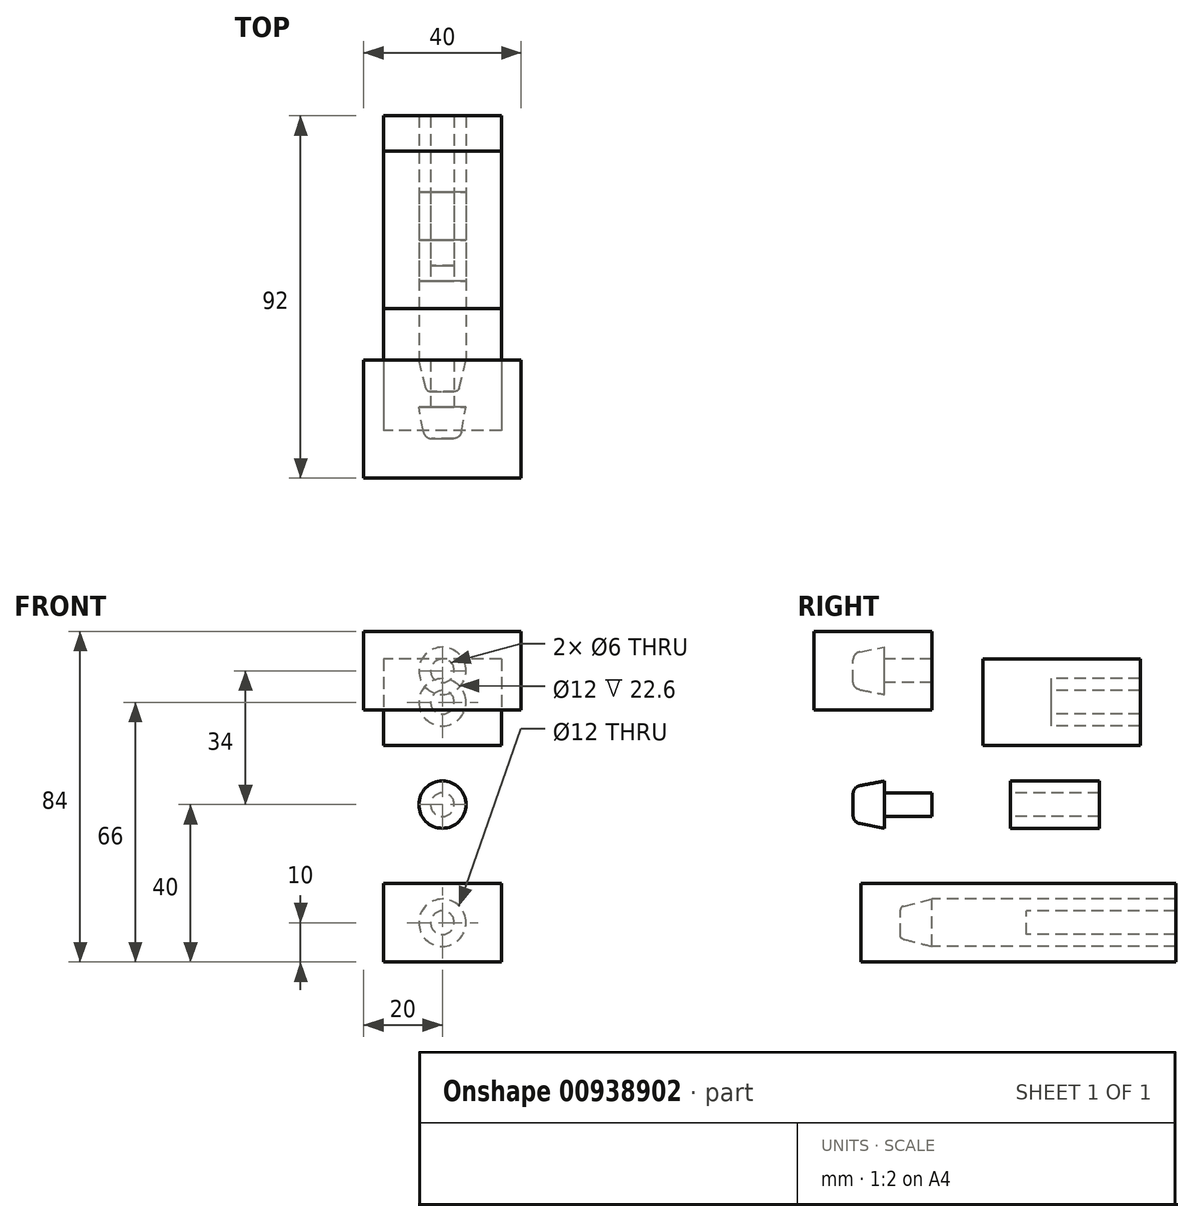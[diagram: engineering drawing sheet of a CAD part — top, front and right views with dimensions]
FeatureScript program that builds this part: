
annotation { "Feature Type Name" : "Feature", "Feature Type Description" : "" }
export const myFeature = defineFeature(function(context is Context, id is Id, definition is map)
    precondition{}
    {
        {
            var Q0;
            Q0=qCreatedBy(makeId("Right.planeOp"),FACE);
            var sketch = newSketch(context, id + "F0", { "sketchPlane" : qUnion([Q0])});
            skLineSegment(sketch, "E0.bottom", {"start": v(0, 0) * mm, "end": v(-12, 0) * mm});
            skLineSegment(sketch, "E0.top", {"start": v(0, 3) * mm, "end": v(-12, 3) * mm});
            skLineSegment(sketch, "E0.left", {"start": v(0, 0) * mm, "end": v(0, 3) * mm});
            skLineSegment(sketch, "E0.right", {"start": v(-12, 0) * mm, "end": v(-12, 3) * mm});
            skLineSegment(sketch, "E1.bottom", {"start": v(-12, 0) * mm, "end": v(-20, 0) * mm});
            skLineSegment(sketch, "E1.left", {"start": v(-12, 0) * mm, "end": v(-12, 6) * mm});
            skLineSegment(sketch, "E1.right", {"start": v(-20, 0) * mm, "end": v(-20, 4.5) * mm});
            skLineSegment(sketch, "E2", {"start": v(-12, 6) * mm, "end": v(-20, 4.5) * mm});
            skLineSegment(sketch, "E3", {"start": v(-20, 4.5) * mm, "end": v(-20, 6) * mm, "construction": true});
            skLineSegment(sketch, "E4", {"start": v(-20, 6) * mm, "end": v(-12, 6) * mm, "construction": true});
            skSolve(sketch);
        }
        {
            var Q0;
            Q0=makeQuery(id+"F0.imprint","IMPRINT",FACE,{"disambiguationData":[TD([[makeQuery(id+"F0.imprint","IMPRINT",EDGE,{"derivedFrom":sQuery(id+"F0.wireOp",EDGE,"E0.right")}),1.0]])]});
            var Q1;
            Q1=makeQuery(id+"F0.imprint","IMPRINT",FACE,{"disambiguationData":[TD([[makeQuery(id+"F0.imprint","IMPRINT",EDGE,{"derivedFrom":sQuery(id+"F0.wireOp",EDGE,"E0.bottom")}),-1.0]])]});
            var Q2;
            Q2=sQuery(id+"F0.wireOp",EDGE,"E0.bottom");
            revolve(context, id + "F1", {"surfaceOperationType" : NewSurfaceOperationType.NEW, "entities" : qUnion([Q0, Q1]), "axis" : qUnion([Q2]), "revolveType" : RevolveType.FULL});
        }
        {
            var Q0;
            Q0=qCreatedBy(makeId("Right.planeOp"),FACE);
            var sketch = newSketch(context, id + "F2", { "sketchPlane" : qUnion([Q0])});
            skLineSegment(sketch, "E5.bottom", {"start": v(20, 0) * mm, "end": v(42.6, 0) * mm});
            skLineSegment(sketch, "E5.top", {"start": v(20, 6) * mm, "end": v(42.6, 6) * mm});
            skLineSegment(sketch, "E5.left", {"start": v(20, 0) * mm, "end": v(20, 6) * mm});
            skLineSegment(sketch, "E5.right", {"start": v(42.6, 0) * mm, "end": v(42.6, 6) * mm});
            skLineSegment(sketch, "E6.top", {"start": v(20, 3) * mm, "end": v(42.6, 3) * mm});
            skLineSegment(sketch, "E6.left", {"start": v(20, 0) * mm, "end": v(20, 3) * mm});
            skLineSegment(sketch, "E6.right", {"start": v(42.6, 0) * mm, "end": v(42.6, 3) * mm});
            skSolve(sketch);
        }
        {
            var Q0;
            {var subQ0=sQuery(id+"F2.wireOp",EDGE,"E5.top");Q0=makeQuery(id+"F2.imprint","IMPRINT",FACE,{"disambiguationData":[TD([[makeQuery(id+"F2.imprint","IMPRINT",EDGE,{"derivedFrom":subQ0}),-1.0]])]});}
            var Q1;
            Q1=sQuery(id+"F2.wireOp",EDGE,"E5.bottom");
            revolve(context, id + "F3", {"surfaceOperationType" : NewSurfaceOperationType.NEW, "entities" : qUnion([Q0]), "axis" : qUnion([Q1]), "revolveType" : RevolveType.FULL});
        }
        {
            var Q0;
            Q0=qCreatedBy(makeId("Right.planeOp"),FACE);
            var sketch = newSketch(context, id + "F4", { "sketchPlane" : qUnion([Q0])});
            skLineSegment(sketch, "E7.bottom", {"start": v(0, 24) * mm, "end": v(-30, 24) * mm});
            skLineSegment(sketch, "E7.top", {"start": v(0, 44) * mm, "end": v(-30, 44) * mm});
            skLineSegment(sketch, "E7.left", {"start": v(0, 24) * mm, "end": v(0, 44) * mm});
            skLineSegment(sketch, "E7.right", {"start": v(-30, 24) * mm, "end": v(-30, 44) * mm});
            skLineSegment(sketch, "E8", {"start": v(0, 34) * mm, "end": v(-30, 34) * mm});
            skLineSegment(sketch, "E9.bottom", {"start": v(0, 34) * mm, "end": v(-12, 34) * mm});
            skLineSegment(sketch, "E9.top", {"start": v(0, 37) * mm, "end": v(-12, 37) * mm});
            skLineSegment(sketch, "E9.left", {"start": v(0, 34) * mm, "end": v(0, 37) * mm});
            skLineSegment(sketch, "E9.right", {"start": v(-12, 34) * mm, "end": v(-12, 37) * mm});
            skLineSegment(sketch, "E10.bottom", {"start": v(-12, 34) * mm, "end": v(0, 34) * mm});
            skLineSegment(sketch, "E10.top", {"start": v(-12, 32.5) * mm, "end": v(0, 32.5) * mm});
            skLineSegment(sketch, "E10.left", {"start": v(-12, 34) * mm, "end": v(-12, 32.5) * mm});
            skLineSegment(sketch, "E10.right", {"start": v(0, 34) * mm, "end": v(0, 32.5) * mm});
            skLineSegment(sketch, "E11.bottom", {"start": v(-12, 34) * mm, "end": v(-20, 34) * mm});
            skLineSegment(sketch, "E11.top", {"start": v(-12, 40) * mm, "end": v(-20, 40) * mm, "construction": true});
            skLineSegment(sketch, "E11.left", {"start": v(-12, 34) * mm, "end": v(-12, 40) * mm});
            skLineSegment(sketch, "E11.right", {"start": v(-20, 34) * mm, "end": v(-20, 38.5) * mm});
            skLineSegment(sketch, "E12", {"start": v(-12, 40) * mm, "end": v(-20, 38.5) * mm});
            skLineSegment(sketch, "E13", {"start": v(-20, 38.5) * mm, "end": v(-20, 40) * mm, "construction": true});
            skSolve(sketch);
        }
        {
            var Q0;
            {var subQ5=sQuery(id+"F4.wireOp",EDGE,"E7.top");Q0=makeQuery(id+"F4.imprint","IMPRINT",FACE,{"disambiguationData":[TD([[makeQuery(id+"F4.imprint","IMPRINT",EDGE,{"derivedFrom":subQ5}),1.0]])]});}
            var Q1;
            {var subQ4=sQuery(id+"F4.wireOp",EDGE,"E7.bottom");Q1=makeQuery(id+"F4.imprint","IMPRINT",FACE,{"disambiguationData":[TD([[makeQuery(id+"F4.imprint","IMPRINT",EDGE,{"derivedFrom":subQ4}),-1.0]])]});}
            var Q2;
            {var subQ3=sQuery(id+"F4.wireOp",EDGE,"E10.top");Q2=makeQuery(id+"F4.imprint","IMPRINT",FACE,{"disambiguationData":[TD([[makeQuery(id+"F4.imprint","IMPRINT",EDGE,{"derivedFrom":subQ3}),1.0]])]});}
            var Q3;
            {var subQ1=sQuery(id+"F4.wireOp",EDGE,"E9.right");Q3=makeQuery(id+"F4.imprint","IMPRINT",FACE,{"disambiguationData":[TD([[makeQuery(id+"F4.imprint","IMPRINT",EDGE,{"derivedFrom":subQ1}),1.0]])]});}
            var Q4;
            {var subQ3=sQuery(id+"F4.wireOp",EDGE,"E9.top");Q4=makeQuery(id+"F4.imprint","IMPRINT",FACE,{"disambiguationData":[TD([[makeQuery(id+"F4.imprint","IMPRINT",EDGE,{"derivedFrom":subQ3}),1.0]])]});}
            extrude(context, id + "F5", {"entities" : qUnion([Q0, Q1, Q2, Q3, Q4]), "depth" : 40 * mm, "offsetDistance" : 25 * mm, "symmetric" : true});
        }
        {
            var Q0;
            {var subQ1=sQuery(id+"F4.wireOp",EDGE,"E9.right");Q0=makeQuery(id+"F4.imprint","IMPRINT",FACE,{"disambiguationData":[TD([[makeQuery(id+"F4.imprint","IMPRINT",EDGE,{"derivedFrom":subQ1}),1.0]])]});}
            var Q1;
            {var subQ3=sQuery(id+"F4.wireOp",EDGE,"E9.top");Q1=makeQuery(id+"F4.imprint","IMPRINT",FACE,{"disambiguationData":[TD([[makeQuery(id+"F4.imprint","IMPRINT",EDGE,{"derivedFrom":subQ3}),1.0]])]});}
            var Q2;
            Q2=sQuery(id+"F4.wireOp",EDGE,"E8");
            revolve(context, id + "F6", {"operationType" : NewBodyOperationType.REMOVE, "surfaceOperationType" : NewSurfaceOperationType.NEW, "entities" : qUnion([Q0, Q1]), "axis" : qUnion([Q2]), "revolveType" : RevolveType.FULL, "oppositeDirection" : true});
        }
        {
            var Q0;
            Q0=qCreatedBy(makeId("Right.planeOp"),FACE);
            var sketch = newSketch(context, id + "F7", { "sketchPlane" : qUnion([Q0])});
            skLineSegment(sketch, "E14.bottom", {"start": v(13, 37) * mm, "end": v(53, 37) * mm});
            skLineSegment(sketch, "E14.top", {"start": v(13, 15) * mm, "end": v(53, 15) * mm});
            skLineSegment(sketch, "E14.left", {"start": v(13, 37) * mm, "end": v(13, 15) * mm});
            skLineSegment(sketch, "E14.right", {"start": v(53, 37) * mm, "end": v(53, 15) * mm});
            skLineSegment(sketch, "E15.bottom", {"start": v(53, 26) * mm, "end": v(30.4, 26) * mm});
            skLineSegment(sketch, "E15.top", {"start": v(53, 32) * mm, "end": v(30.4, 32) * mm});
            skLineSegment(sketch, "E15.left", {"start": v(53, 26) * mm, "end": v(53, 32) * mm});
            skLineSegment(sketch, "E15.right", {"start": v(30.4, 26) * mm, "end": v(30.4, 32) * mm});
            skLineSegment(sketch, "E16", {"start": v(53, 29) * mm, "end": v(30.4, 29) * mm});
            skSolve(sketch);
        }
        {
            var Q0;
            {var subQ3=sQuery(id+"F7.wireOp",EDGE,"E14.bottom");Q0=makeQuery(id+"F7.imprint","IMPRINT",FACE,{"disambiguationData":[TD([[makeQuery(id+"F7.imprint","IMPRINT",EDGE,{"derivedFrom":subQ3}),-1.0]])]});}
            var Q1;
            {var subQ0=sQuery(id+"F7.wireOp",EDGE,"E15.bottom");Q1=makeQuery(id+"F7.imprint","IMPRINT",FACE,{"disambiguationData":[TD([[makeQuery(id+"F7.imprint","IMPRINT",EDGE,{"derivedFrom":subQ0}),-1.0]])]});}
            var Q2;
            {var subQ0=sQuery(id+"F7.wireOp",EDGE,"E15.top");Q2=makeQuery(id+"F7.imprint","IMPRINT",FACE,{"disambiguationData":[TD([[makeQuery(id+"F7.imprint","IMPRINT",EDGE,{"derivedFrom":subQ0}),1.0]])]});}
            extrude(context, id + "F8", {"entities" : qUnion([Q0, Q1, Q2]), "depth" : 30 * mm, "offsetDistance" : 25 * mm, "symmetric" : true});
        }
        {
            var Q0;
            {var subQ0=sQuery(id+"F7.wireOp",EDGE,"E15.top");Q0=makeQuery(id+"F7.imprint","IMPRINT",FACE,{"disambiguationData":[TD([[makeQuery(id+"F7.imprint","IMPRINT",EDGE,{"derivedFrom":subQ0}),1.0]])]});}
            var Q1;
            Q1=sQuery(id+"F7.wireOp",EDGE,"E15.bottom");
            revolve(context, id + "F9", {"operationType" : NewBodyOperationType.REMOVE, "surfaceOperationType" : NewSurfaceOperationType.NEW, "entities" : qUnion([Q0]), "axis" : qUnion([Q1]), "revolveType" : RevolveType.FULL, "oppositeDirection" : true});
        }
        {
            var Q0;
            Q0=makeQuery(id+"F6.boolean.opBoolean","COPY",EDGE,{"derivedFrom":makeQuery(id+"F6.opRevolve","SWEPT_EDGE",EDGE,{"disambiguationData":[OSD([sQuery(id+"F4.wireOp",EDGE,"E11.right"),sQuery(id+"F4.wireOp",EDGE,"E12")])]})});
            var Q1;
            Q1=makeQuery(id+"F1.opRevolve","SWEPT_EDGE",EDGE,{"disambiguationData":[OSD([sQuery(id+"F0.wireOp",EDGE,"E1.right"),sQuery(id+"F0.wireOp",EDGE,"E2")])]});
            fillet(context, id + "F10", {"entities" : qUnion([Q0, Q1]), "radius" : 2.1 * mm, "tangentPropagation" : true, "allowEdgeOverflow" : false});
        }
        {
            var Q0;
            Q0=qCreatedBy(makeId("Right.planeOp"),FACE);
            var sketch = newSketch(context, id + "F11", { "sketchPlane" : qUnion([Q0])});
            skLineSegment(sketch, "E17.bottom", {"start": v(0, -24) * mm, "end": v(62, -24) * mm});
            skLineSegment(sketch, "E17.top", {"start": v(0, -30) * mm, "end": v(62, -30) * mm});
            skLineSegment(sketch, "E17.left", {"start": v(0, -24) * mm, "end": v(0, -30) * mm});
            skLineSegment(sketch, "E17.right", {"start": v(62, -24) * mm, "end": v(62, -30) * mm});
            skLineSegment(sketch, "E18.top", {"start": v(0, -27) * mm, "end": v(62, -27) * mm});
            skLineSegment(sketch, "E18.left", {"start": v(0, -24) * mm, "end": v(0, -27) * mm});
            skLineSegment(sketch, "E18.right", {"start": v(62, -24) * mm, "end": v(62, -27) * mm});
            skLineSegment(sketch, "E19.bottom", {"start": v(0, -24) * mm, "end": v(-8, -24) * mm, "construction": true});
            skLineSegment(sketch, "E19.top", {"start": v(0, -30) * mm, "end": v(-8, -30) * mm});
            skLineSegment(sketch, "E19.right", {"start": v(-8, -26.78) * mm, "end": v(-8, -30) * mm});
            skLineSegment(sketch, "E20.bottom", {"start": v(0, -27) * mm, "end": v(24, -27) * mm});
            skLineSegment(sketch, "E20.top", {"start": v(0, -30) * mm, "end": v(24, -30) * mm});
            skLineSegment(sketch, "E20.left", {"start": v(0, -27) * mm, "end": v(0, -30) * mm});
            skLineSegment(sketch, "E20.right", {"start": v(24, -27) * mm, "end": v(24, -30) * mm});
            skLineSegment(sketch, "E21", {"start": v(0, -24) * mm, "end": v(-7.24, -25.81) * mm});
            skLineSegment(sketch, "E22", {"start": v(-8, -26) * mm, "end": v(-8, -24) * mm, "construction": true});
            skPoint(sketch, "E23.visualSharp", {"position": v(-8, -26) * mm});
            skArc(sketch, "E23.filletArc", {"start": v(-7.24, -25.81) * mm, "mid": v(-7.79, -26.17) * mm, "end": v(-8, -26.78) * mm});
            skLineSegment(sketch, "E24.bottom", {"start": v(62, -30) * mm, "end": v(-18, -30) * mm});
            skLineSegment(sketch, "E24.top", {"start": v(62, -20) * mm, "end": v(-18, -20) * mm});
            skLineSegment(sketch, "E24.left", {"start": v(62, -30) * mm, "end": v(62, -20) * mm});
            skLineSegment(sketch, "E24.right", {"start": v(-18, -30) * mm, "end": v(-18, -20) * mm});
            skLineSegment(sketch, "E25.MirrorCS", {"start": v(62, -40) * mm, "end": v(-18, -40) * mm});
            skLineSegment(sketch, "E26.MirrorCS", {"start": v(-18, -30) * mm, "end": v(-18, -40) * mm});
            skLineSegment(sketch, "E27.MirrorCS", {"start": v(62, -30) * mm, "end": v(62, -40) * mm});
            skSolve(sketch);
        }
        {
            var Q0;
            {var subQ0=sQuery(id+"F11.wireOp",EDGE,"E20.right");var subQ8=sQuery(id+"F11.wireOp",EDGE,"E17.bottom");var subQ11=makeQuery(id+"F11.imprint","IMPRINT",EDGE,{"derivedFrom":subQ8});var subQ18=sQuery(id+"F11.wireOp",EDGE,"E19.top");Q0=qUnion([makeQuery(id+"F11.imprint","IMPRINT",FACE,{"disambiguationData":[TD([[makeQuery(id+"F11.imprint","IMPRINT",EDGE,{"derivedFrom":subQ18}),1.0]])]}),makeQuery(id+"F11.imprint","IMPRINT",FACE,{"disambiguationData":[TD([[subQ11,1.0]])]}),makeQuery(id+"F11.imprint","IMPRINT",FACE,{"disambiguationData":[TD([[makeQuery(id+"F11.imprint","IMPRINT",EDGE,{"derivedFrom":subQ0}),1.0]])]}),makeQuery(id+"F11.imprint","IMPRINT",FACE,{"disambiguationData":[TD([[subQ11,-1.0]])]})]);}
            var Q1;
            {var subQ0=sQuery(id+"F11.wireOp",EDGE,"E19.top");Q1=makeQuery(id+"F11.imprint","IMPRINT",FACE,{"disambiguationData":[TD([[makeQuery(id+"F11.imprint","IMPRINT",EDGE,{"derivedFrom":subQ0}),-1.0]])]});}
            var Q2;
            {var subQ0=sQuery(id+"F11.wireOp",EDGE,"E20.right");Q2=makeQuery(id+"F11.imprint","IMPRINT",FACE,{"disambiguationData":[TD([[makeQuery(id+"F11.imprint","IMPRINT",EDGE,{"derivedFrom":subQ0}),-1.0]])]});}
            extrude(context, id + "F12", {"entities" : qUnion([Q0, Q1, Q2]), "depth" : 30 * mm, "offsetDistance" : 25 * mm, "symmetric" : true});
        }
        {
            var Q0;
            {var subQ0=sQuery(id+"F11.wireOp",EDGE,"E19.top");Q0=makeQuery(id+"F11.imprint","IMPRINT",FACE,{"disambiguationData":[TD([[makeQuery(id+"F11.imprint","IMPRINT",EDGE,{"derivedFrom":subQ0}),-1.0]])]});}
            var Q1;
            {var subQ0=sQuery(id+"F11.wireOp",EDGE,"E20.right");Q1=makeQuery(id+"F11.imprint","IMPRINT",FACE,{"disambiguationData":[TD([[makeQuery(id+"F11.imprint","IMPRINT",EDGE,{"derivedFrom":subQ0}),-1.0]])]});}
            var Q2;
            {var subQ5=sQuery(id+"F11.wireOp",EDGE,"E17.bottom");Q2=makeQuery(id+"F11.imprint","IMPRINT",FACE,{"disambiguationData":[TD([[makeQuery(id+"F11.imprint","IMPRINT",EDGE,{"derivedFrom":subQ5}),-1.0]])]});}
            var Q3;
            Q3=sQuery(id+"F11.wireOp",EDGE,"E24.bottom");
            revolve(context, id + "F13", {"operationType" : NewBodyOperationType.REMOVE, "surfaceOperationType" : NewSurfaceOperationType.NEW, "entities" : qUnion([Q0, Q1, Q2]), "axis" : qUnion([Q3]), "revolveType" : RevolveType.FULL, "oppositeDirection" : true});
        }
    });
